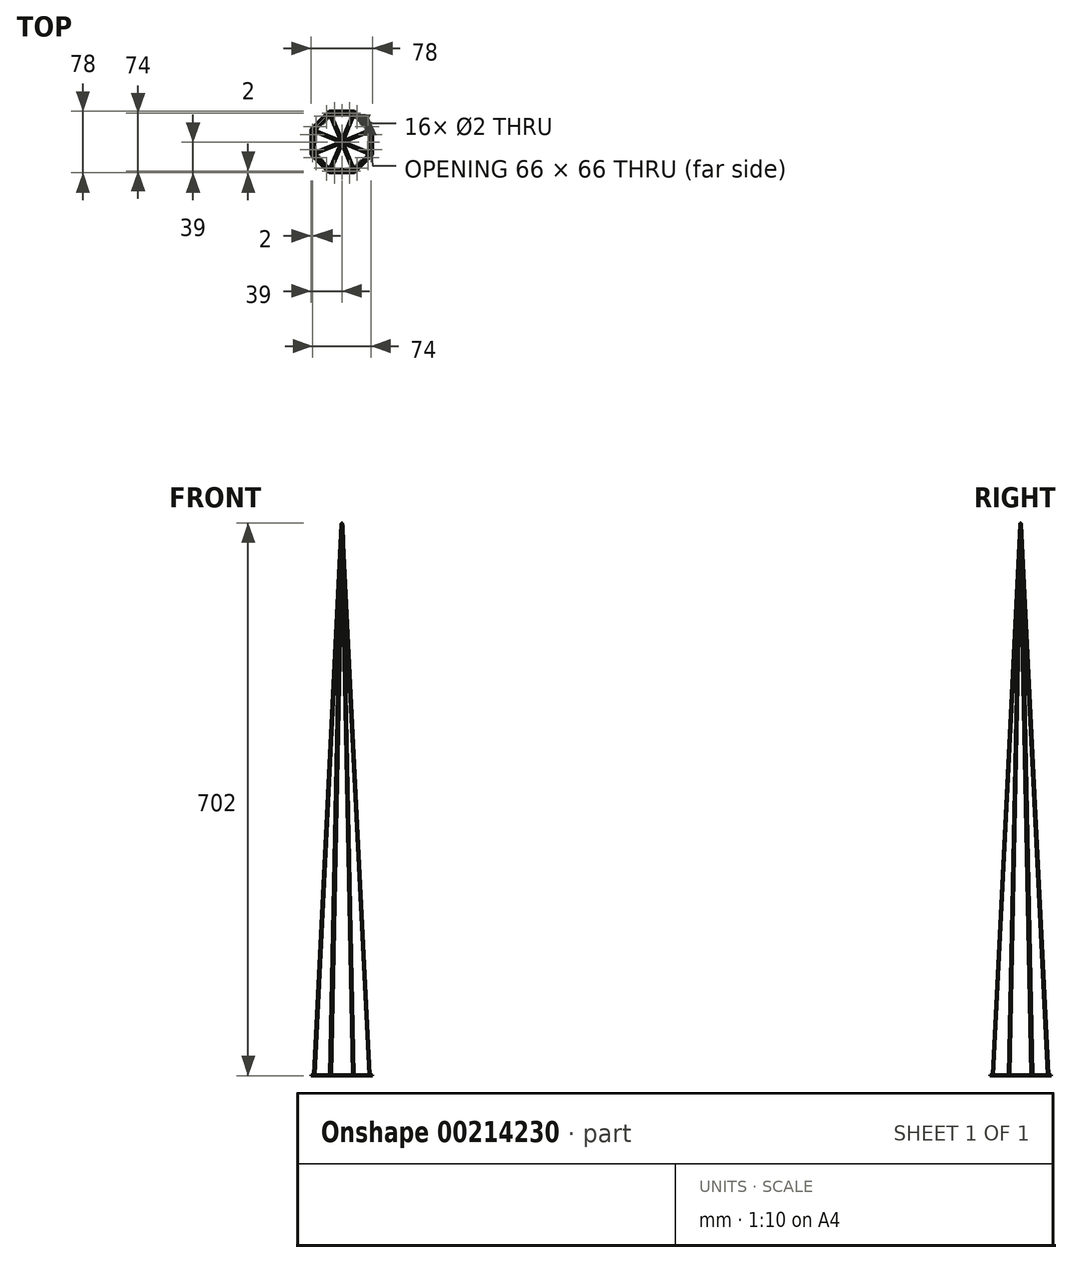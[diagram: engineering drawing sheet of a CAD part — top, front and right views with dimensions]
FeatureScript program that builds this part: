
annotation { "Feature Type Name" : "Feature", "Feature Type Description" : "" }
export const myFeature = defineFeature(function(context is Context, id is Id, definition is map)
    precondition{}
    {
        {
            var Q0;
            Q0=qCreatedBy(makeId("Top.planeOp"),FACE);
            var sketch = newSketch(context, id + "F0", { "sketchPlane" : qUnion([Q0])});
            skCircle(sketch, "E0.cCircle", {"center": v(0, 0) * mm, "radius": 35 * mm, "construction": true});
            skLineSegment(sketch, "E0.0", {"start": v(-14.5, 35) * mm, "end": v(14.5, 35) * mm});
            skLineSegment(sketch, "E0.1", {"start": v(14.5, 35) * mm, "end": v(35, 14.5) * mm});
            skLineSegment(sketch, "E0.2", {"start": v(35, 14.5) * mm, "end": v(35, -14.5) * mm});
            skLineSegment(sketch, "E0.3", {"start": v(35, -14.5) * mm, "end": v(14.5, -35) * mm});
            skLineSegment(sketch, "E0.4", {"start": v(14.5, -35) * mm, "end": v(-14.5, -35) * mm});
            skLineSegment(sketch, "E0.5", {"start": v(-14.5, -35) * mm, "end": v(-35, -14.5) * mm});
            skLineSegment(sketch, "E0.6", {"start": v(-35, -14.5) * mm, "end": v(-35, 14.5) * mm});
            skLineSegment(sketch, "E0.7", {"start": v(-35, 14.5) * mm, "end": v(-14.5, 35) * mm});
            skPoint(sketch, "E0.0.midPoint", {"position": v(0, 35) * mm});
            skSolve(sketch);
        }
        {
            var Q0;
            Q0=qCreatedBy(makeId("Top.planeOp"),FACE);
            cPlane(context, id + "F1", {"entities" : qUnion([Q0]), "cplaneType" : CPlaneType.OFFSET, "offset" : 700 * mm, "width" : 150 * mm, "height" : 150 * mm});
        }
        {
            var Q0;
            Q0=qCreatedBy(id+"F1.planeOp",FACE);
            var sketch = newSketch(context, id + "F2", { "sketchPlane" : qUnion([Q0])});
            skPoint(sketch, "E1", {"position": v(0, 0) * mm});
            skSolve(sketch);
        }
        {
            var Q0;
            Q0=makeQuery(id+"F0.imprint","IMPRINT",FACE,{"disambiguationData":[TD([[makeQuery(id+"F0.imprint","IMPRINT",EDGE,{"derivedFrom":sQuery(id+"F0.wireOp",EDGE,"E0.0")}),-1.0]])]});
            var Q1;
            Q1=sQuery(id+"F2.wireOp",VERTEX,"E1");
            loft(context, id + "F3", {"sheetProfilesArray" : [{ "sheetProfileEntities" : qUnion([Q0]) }, { "sheetProfileEntities" : qUnion([Q1]) }]});
        }
        {
            var Q0;
            Q0=makeQuery(id+"F3.opLoft","SWEPT_FACE",FACE,{"disambiguationData":[OSD([sQuery(id+"F0.wireOp",EDGE,"E0.3"),sQuery(id+"F0.wireOp",EDGE,"E0.4"),sQuery(id+"F0.wireOp",EDGE,"E0.5")])]});
            var sketch = newSketch(context, id + "F4", { "sketchPlane" : qUnion([Q0])});
            skLineSegment(sketch, "E2.0", {"start": v(-14.5, -1.75) * mm, "end": v(0, 699.13) * mm});
            skArc(sketch, "E3", {"start": v(1, 699.1) * mm, "mid": v(0.72, 699.82) * mm, "end": v(0.02, 700.13) * mm});
            skArc(sketch, "E4", {"start": v(-14.52, -2.75) * mm, "mid": v(-13.8, -2.47) * mm, "end": v(-13.5, -1.77) * mm});
            skLineSegment(sketch, "E5", {"start": v(1, 699.1) * mm, "end": v(-13.5, -1.77) * mm});
            skLineSegment(sketch, "E6", {"start": v(-14.52, -2.75) * mm, "end": v(0.02, 700.13) * mm});
            skSolve(sketch);
        }
        {
            var Q0;
            Q0 = qSketchRegion(id + "F4", true);
            var Q1;
            Q1=sQuery(id+"F4.wireOp",EDGE,"E6");
            revolve(context, id + "F5", {"entities" : qUnion([Q0]), "axis" : qUnion([Q1]), "revolveType" : RevolveType.FULL});
        }
        {
            var Q0;
            Q0=qCreatedBy(makeId("Top.planeOp"),FACE);
            var sketch = newSketch(context, id + "F6", { "sketchPlane" : qUnion([Q0])});
            skCircle(sketch, "E7", {"center": v(0, 0) * mm, "radius": 73 * mm});
            skSolve(sketch);
        }
        {
            var Q0;
            Q0=makeQuery(id+"F3.opLoft","CAP_FACE",FACE,{"disambiguationData":[OSD([makeQuery(id+"F0.imprint","IMPRINT",FACE,{"disambiguationData":[TD([[makeQuery(id+"F0.imprint","IMPRINT",EDGE,{"derivedFrom":sQuery(id+"F0.wireOp",EDGE,"E0.0")}),-1.0]])]})])],"isStart":true});
            shell(context, id + "F7", {"entities" : qUnion([Q0]), "thickness" : 0.8 * mm});
        }
        {
            var Q0;
            Q0=makeQuery(id+"F5.opRevolve","SWEPT_BODY",BODY,{"disambiguationData":[OSD([sQuery(id+"F4.wireOp",EDGE,"E3"),sQuery(id+"F4.wireOp",EDGE,"E4"),sQuery(id+"F4.wireOp",EDGE,"E5"),sQuery(id+"F4.wireOp",EDGE,"E6")])]});
            var Q1;
            Q1=sQuery(id+"F6.wireOp",EDGE,"E7");
            circularPattern(context, id + "F8", {"operationType" : NewBodyOperationType.ADD, "entities" : qUnion([Q0]), "axis" : qUnion([Q1]), "angle" : 360 * degree, "instanceCount" : 8, "equalSpace" : true});
        }
        {
            var Q0;
            Q0=qCreatedBy(makeId("Front.planeOp"),FACE);
            var sketch = newSketch(context, id + "F9", { "sketchPlane" : qUnion([Q0])});
            skLineSegment(sketch, "E8.bottom", {"start": v(-66.46, 0) * mm, "end": v(133.9, 0) * mm});
            skLineSegment(sketch, "E8.top", {"start": v(-66.46, -54.17) * mm, "end": v(133.9, -54.17) * mm});
            skLineSegment(sketch, "E8.left", {"start": v(-66.46, 0) * mm, "end": v(-66.46, -54.17) * mm});
            skLineSegment(sketch, "E8.right", {"start": v(133.9, 0) * mm, "end": v(133.9, -54.17) * mm});
            skSolve(sketch);
        }
        {
            var Q0;
            Q0 = qSketchRegion(id + "F9", true);
            extrude(context, id + "F10", {"entities" : qUnion([Q0]), "operationType" : NewBodyOperationType.REMOVE, "endBound" : BoundingType.SYMMETRIC, "oppositeDirection" : true, "depth" : 200 * mm});
        }
        {
            var Q0;
            Q0=qCreatedBy(makeId("Top.planeOp"),FACE);
            var sketch = newSketch(context, id + "F11", { "sketchPlane" : qUnion([Q0])});
            skCircle(sketch, "E9.cCircle", {"center": v(0, 0) * mm, "radius": 39 * mm, "construction": true});
            skLineSegment(sketch, "E9.0", {"start": v(-16.15, 39) * mm, "end": v(16.15, 39) * mm});
            skLineSegment(sketch, "E9.1", {"start": v(16.15, 39) * mm, "end": v(39, 16.15) * mm});
            skLineSegment(sketch, "E9.2", {"start": v(39, 16.15) * mm, "end": v(39, -16.15) * mm});
            skLineSegment(sketch, "E9.3", {"start": v(39, -16.15) * mm, "end": v(16.15, -39) * mm});
            skLineSegment(sketch, "E9.4", {"start": v(16.15, -39) * mm, "end": v(-16.15, -39) * mm});
            skLineSegment(sketch, "E9.5", {"start": v(-16.15, -39) * mm, "end": v(-39, -16.15) * mm});
            skLineSegment(sketch, "E9.6", {"start": v(-39, -16.15) * mm, "end": v(-39, 16.15) * mm});
            skLineSegment(sketch, "E9.7", {"start": v(-39, 16.15) * mm, "end": v(-16.15, 39) * mm});
            skPoint(sketch, "E9.0.midPoint", {"position": v(0, 39) * mm});
            skSolve(sketch);
        }
        {
            var Q0;
            Q0 = qSketchRegion(id + "F11", true);
            extrude(context, id + "F12", {"entities" : qUnion([Q0]), "operationType" : NewBodyOperationType.ADD, "oppositeDirection" : true, "depth" : 1 * mm});
        }
        {
            var Q0;
            Q0=makeQuery(id+"F12.opExtrude","CAP_FACE",FACE,{"disambiguationData":[OSD([sQuery(id+"F11.wireOp",EDGE,"E9.0"),sQuery(id+"F11.wireOp",EDGE,"E9.1"),sQuery(id+"F11.wireOp",EDGE,"E9.2"),sQuery(id+"F11.wireOp",EDGE,"E9.3"),sQuery(id+"F11.wireOp",EDGE,"E9.4"),sQuery(id+"F11.wireOp",EDGE,"E9.5"),sQuery(id+"F11.wireOp",EDGE,"E9.6"),sQuery(id+"F11.wireOp",EDGE,"E9.7")])],"isStart":false});
            var sketch = newSketch(context, id + "F13", { "sketchPlane" : qUnion([Q0])});
            skCircle(sketch, "E10.cCircle", {"center": v(0, 0) * mm, "radius": 33 * mm, "construction": true});
            skLineSegment(sketch, "E10.0", {"start": v(-13.67, 33) * mm, "end": v(13.67, 33) * mm});
            skLineSegment(sketch, "E10.1", {"start": v(13.67, 33) * mm, "end": v(33, 13.67) * mm});
            skLineSegment(sketch, "E10.2", {"start": v(33, 13.67) * mm, "end": v(33, -13.67) * mm});
            skLineSegment(sketch, "E10.3", {"start": v(33, -13.67) * mm, "end": v(13.67, -33) * mm});
            skLineSegment(sketch, "E10.4", {"start": v(13.67, -33) * mm, "end": v(-13.67, -33) * mm});
            skLineSegment(sketch, "E10.5", {"start": v(-13.67, -33) * mm, "end": v(-33, -13.67) * mm});
            skLineSegment(sketch, "E10.6", {"start": v(-33, -13.67) * mm, "end": v(-33, 13.67) * mm});
            skLineSegment(sketch, "E10.7", {"start": v(-33, 13.67) * mm, "end": v(-13.67, 33) * mm});
            skPoint(sketch, "E10.0.midPoint", {"position": v(0, 33) * mm});
            skSolve(sketch);
        }
        {
            var Q0;
            Q0 = qSketchRegion(id + "F13", true);
            extrude(context, id + "F14", {"entities" : qUnion([Q0]), "operationType" : NewBodyOperationType.REMOVE, "oppositeDirection" : true, "depth" : 1 * mm});
        }
        {
            var Q0;
            {var subQ0=sQuery(id+"F11.wireOp",EDGE,"E9.0");var subQ2=makeQuery(id+"F5.opRevolve","SWEPT_FACE",FACE,{"disambiguationData":[OSD([sQuery(id+"F4.wireOp",EDGE,"E4")])]});var subQ6=sQuery(id+"F11.wireOp",EDGE,"E9.4");var subQ7=sQuery(id+"F11.wireOp",EDGE,"E9.3");var subQ9=sQuery(id+"F11.wireOp",EDGE,"E9.5");var subQ14=sQuery(id+"F11.wireOp",EDGE,"E9.2");var subQ15=sQuery(id+"F11.wireOp",EDGE,"E9.1");var subQ16=sQuery(id+"F11.wireOp",EDGE,"E9.6");var subQ17=sQuery(id+"F11.wireOp",EDGE,"E9.7");Q0=makeQuery(id+"F12.boolean.opBoolean","SPLIT",FACE,{"disambiguationData":[TD([subQ2])],"derivedFrom":makeQuery(id+"F12.opExtrude","CAP_FACE",FACE,{"disambiguationData":[OSD([subQ0,subQ15,subQ14,subQ7,subQ6,subQ9,subQ16,subQ17])],"isStart":true})});}
            var sketch = newSketch(context, id + "F15", { "sketchPlane" : qUnion([Q0])});
            skCircle(sketch, "E11", {"center": v(-9.5, 37) * mm, "radius": 1 * mm});
            skCircle(sketch, "E12", {"center": v(9.5, 37) * mm, "radius": 1 * mm});
            skCircle(sketch, "E13", {"center": v(0, 0) * mm, "radius": 47.33 * mm, "construction": true});
            skCircle(sketch, "E14.1.0", {"center": v(-32.88, 19.45) * mm, "radius": 1 * mm});
            skCircle(sketch, "E14.1.1", {"center": v(-19.45, 32.88) * mm, "radius": 1 * mm});
            skCircle(sketch, "E14.2.0", {"center": v(-37, -9.5) * mm, "radius": 1 * mm});
            skCircle(sketch, "E14.2.1", {"center": v(-37, 9.5) * mm, "radius": 1 * mm});
            skCircle(sketch, "E14.3.0", {"center": v(-19.45, -32.88) * mm, "radius": 1 * mm});
            skCircle(sketch, "E14.3.1", {"center": v(-32.88, -19.45) * mm, "radius": 1 * mm});
            skCircle(sketch, "E14.4.0", {"center": v(9.5, -37) * mm, "radius": 1 * mm});
            skCircle(sketch, "E14.4.1", {"center": v(-9.5, -37) * mm, "radius": 1 * mm});
            skCircle(sketch, "E14.5.0", {"center": v(32.88, -19.45) * mm, "radius": 1 * mm});
            skCircle(sketch, "E14.5.1", {"center": v(19.45, -32.88) * mm, "radius": 1 * mm});
            skCircle(sketch, "E14.6.0", {"center": v(37, 9.5) * mm, "radius": 1 * mm});
            skCircle(sketch, "E14.6.1", {"center": v(37, -9.5) * mm, "radius": 1 * mm});
            skCircle(sketch, "E14.7.0", {"center": v(19.45, 32.88) * mm, "radius": 1 * mm});
            skCircle(sketch, "E14.7.1", {"center": v(32.88, 19.45) * mm, "radius": 1 * mm});
            skSolve(sketch);
        }
        {
            var Q0;
            Q0 = qSketchRegion(id + "F15", true);
            extrude(context, id + "F16", {"entities" : qUnion([Q0]), "operationType" : NewBodyOperationType.REMOVE, "oppositeDirection" : true, "depth" : 25 * mm});
        }
    });
